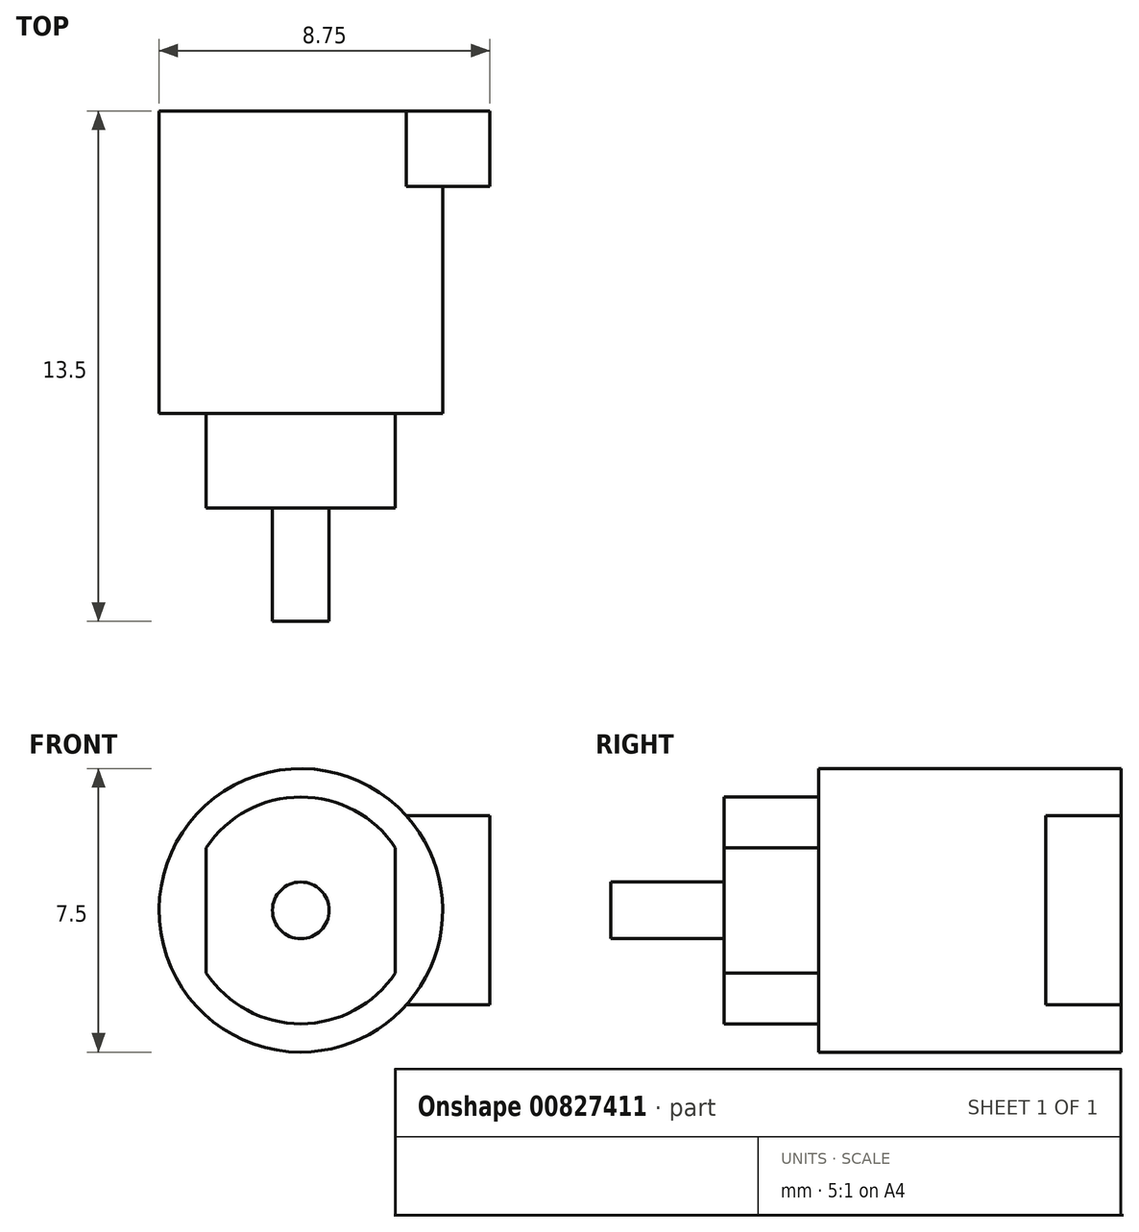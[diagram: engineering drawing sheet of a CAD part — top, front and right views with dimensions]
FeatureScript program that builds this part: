
annotation { "Feature Type Name" : "Feature", "Feature Type Description" : "" }
export const myFeature = defineFeature(function(context is Context, id is Id, definition is map)
    precondition{}
    {
        {
            var Q0;
            Q0=qCreatedBy(makeId("Front.planeOp"),FACE);
            var sketch = newSketch(context, id + "F0", { "sketchPlane" : qUnion([Q0])});
            skCircle(sketch, "E0", {"center": v(0, 0) * mm, "radius": 3.75 * mm});
            skSolve(sketch);
        }
        {
            var Q0;
            Q0=makeQuery(id+"F0.imprint","IMPRINT",FACE,{"disambiguationData":[TD([[makeQuery(id+"F0.imprint","IMPRINT",EDGE,{"derivedFrom":sQuery(id+"F0.wireOp",EDGE,"E0")}),1.0]])]});
            extrude(context, id + "F1", {"entities" : qUnion([Q0]), "depth" : 8 * mm, "offsetDistance" : 25 * mm});
        }
        {
            var Q0;
            Q0=makeQuery(id+"F1.opExtrude","CAP_FACE",FACE,{"disambiguationData":[OSD([sQuery(id+"F0.wireOp",EDGE,"E0")])],"isStart":false});
            var sketch = newSketch(context, id + "F2", { "sketchPlane" : qUnion([Q0])});
            skArc(sketch, "E1", {"start": v(-2.5, -1.66) * mm, "mid": v(0, -3) * mm, "end": v(2.5, -1.66) * mm});
            skLineSegment(sketch, "E2.left", {"start": v(-2.5, 1.66) * mm, "end": v(-2.5, -1.66) * mm});
            skLineSegment(sketch, "E2.right", {"start": v(2.5, 1.66) * mm, "end": v(2.5, -1.66) * mm});
            skArc(sketch, "E3.trimOffspring", {"start": v(2.5, 1.66) * mm, "mid": v(0, 3) * mm, "end": v(-2.5, 1.66) * mm});
            skSolve(sketch);
        }
        {
            var Q0;
            Q0=makeQuery(id+"F2.imprint","IMPRINT",FACE,{"disambiguationData":[TD([[makeQuery(id+"F2.imprint","IMPRINT",EDGE,{"derivedFrom":sQuery(id+"F2.wireOp",EDGE,"E1")}),1.0]])]});
            extrude(context, id + "F3", {"entities" : qUnion([Q0]), "operationType" : NewBodyOperationType.ADD, "depth" : 2.5 * mm, "offsetDistance" : 25 * mm});
        }
        {
            var Q0;
            Q0=makeQuery(id+"F3.opExtrude","CAP_FACE",FACE,{"disambiguationData":[OSD([sQuery(id+"F2.wireOp",EDGE,"E1"),sQuery(id+"F2.wireOp",EDGE,"E2.left"),sQuery(id+"F2.wireOp",EDGE,"E2.right"),sQuery(id+"F2.wireOp",EDGE,"E3.trimOffspring")])],"isStart":false});
            var sketch = newSketch(context, id + "F4", { "sketchPlane" : qUnion([Q0])});
            skCircle(sketch, "E4", {"center": v(0, 0) * mm, "radius": 0.75 * mm});
            skSolve(sketch);
        }
        {
            var Q0;
            Q0=makeQuery(id+"F4.imprint","IMPRINT",FACE,{"disambiguationData":[TD([[makeQuery(id+"F4.imprint","IMPRINT",EDGE,{"derivedFrom":sQuery(id+"F4.wireOp",EDGE,"E4")}),1.0]])]});
            extrude(context, id + "F5", {"entities" : qUnion([Q0]), "operationType" : NewBodyOperationType.ADD, "depth" : 3 * mm, "offsetDistance" : 25 * mm});
        }
        {
            var Q0;
            Q0=makeQuery(id+"F1.opExtrude","CAP_FACE",FACE,{"disambiguationData":[OSD([sQuery(id+"F0.wireOp",EDGE,"E0")])],"isStart":true});
            var sketch = newSketch(context, id + "F6", { "sketchPlane" : qUnion([Q0])});
            skLineSegment(sketch, "E5.bottom", {"start": v(-5, 2.5) * mm, "end": v(0, 2.5) * mm});
            skLineSegment(sketch, "E5.top", {"start": v(-5, -2.5) * mm, "end": v(0, -2.5) * mm});
            skLineSegment(sketch, "E5.left", {"start": v(-5, 2.5) * mm, "end": v(-5, -2.5) * mm});
            skLineSegment(sketch, "E5.right", {"start": v(0, 2.5) * mm, "end": v(0, -2.5) * mm});
            skSolve(sketch);
        }
        {
            var Q0;
            {var subQ0=sQuery(id+"F6.wireOp",EDGE,"Iyi1r8tu-Qd6C-FJwB-9o27-nrpYNpMHR6AU.left");Q0=makeQuery(id+"F6.imprint","IMPRINT",FACE,{"disambiguationData":[TD([[makeQuery(id+"F6.imprint","IMPRINT",EDGE,{"derivedFrom":subQ0}),1.0]])]});}
            var Q1;
            {var subQ0=sQuery(id+"F6.wireOp",EDGE,"Iyi1r8tu-Qd6C-FJwB-9o27-nrpYNpMHR6AU.right");Q1=makeQuery(id+"F6.imprint","IMPRINT",FACE,{"disambiguationData":[TD([[makeQuery(id+"F6.imprint","IMPRINT",EDGE,{"derivedFrom":subQ0}),-1.0]])]});}
            var Q2;
            {var subQ0=sQuery(id+"F6.wireOp",EDGE,"E5.right");Q2=makeQuery(id+"F6.imprint","IMPRINT",FACE,{"disambiguationData":[TD([[makeQuery(id+"F6.imprint","IMPRINT",EDGE,{"derivedFrom":subQ0}),-1.0]])]});}
            var Q3;
            {var subQ0=sQuery(id+"F6.wireOp",EDGE,"E5.left");Q3=makeQuery(id+"F6.imprint","IMPRINT",FACE,{"disambiguationData":[TD([[makeQuery(id+"F6.imprint","IMPRINT",EDGE,{"derivedFrom":subQ0}),1.0]])]});}
            extrude(context, id + "F7", {"entities" : qUnion([Q0, Q1, Q2, Q3]), "operationType" : NewBodyOperationType.ADD, "oppositeDirection" : true, "depth" : 2 * mm, "offsetDistance" : 25 * mm});
        }
    });
